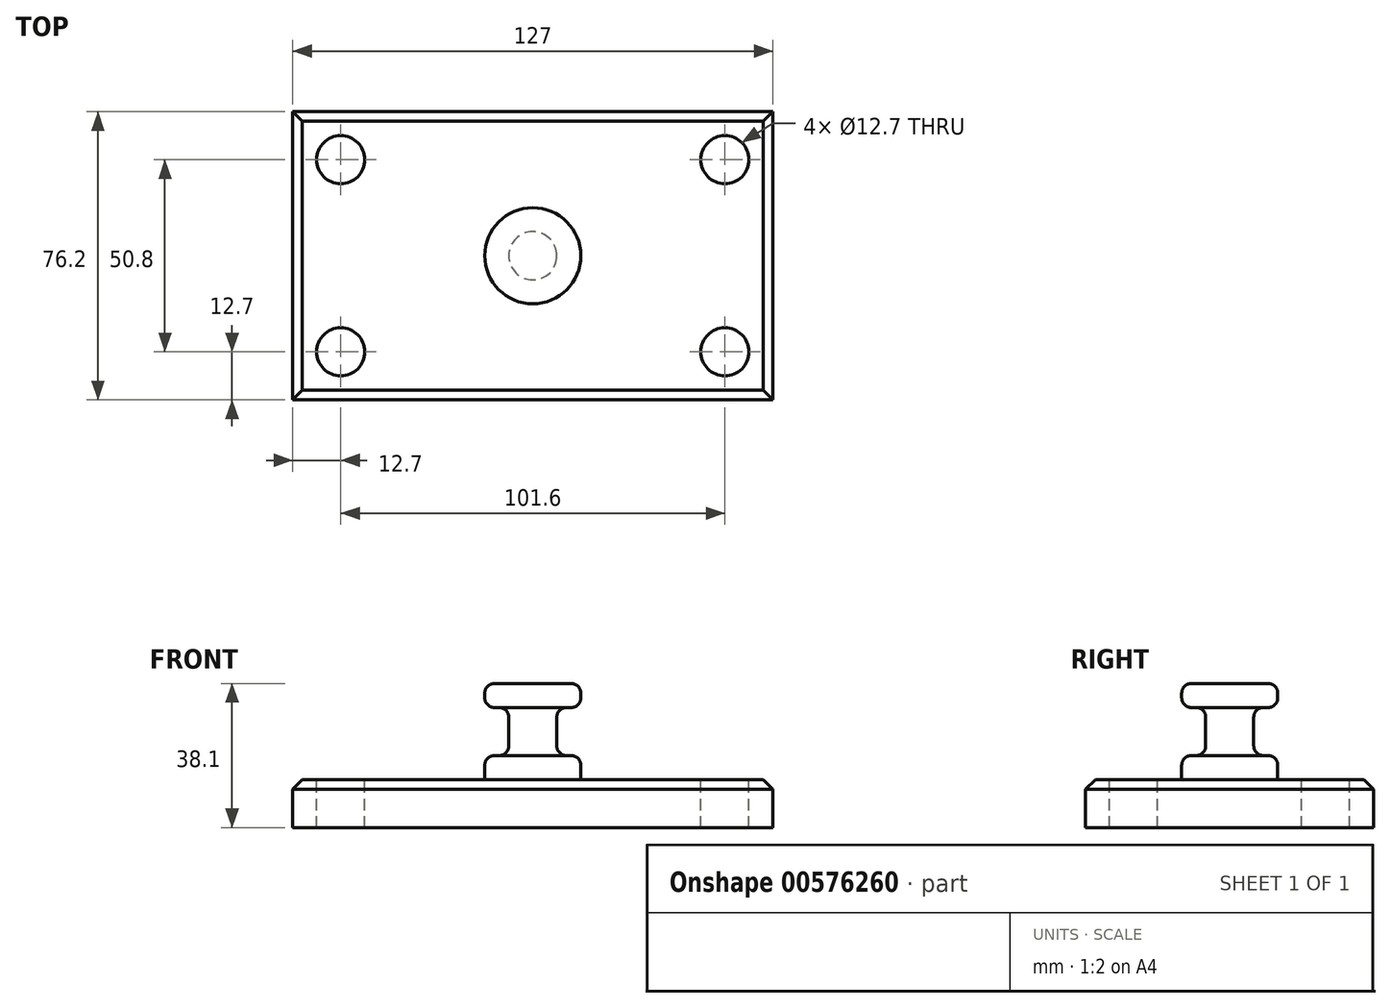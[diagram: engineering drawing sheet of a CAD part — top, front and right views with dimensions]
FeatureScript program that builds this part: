
annotation { "Feature Type Name" : "Feature", "Feature Type Description" : "" }
export const myFeature = defineFeature(function(context is Context, id is Id, definition is map)
    precondition{}
    {
        {
            var Q0;
            Q0=qCreatedBy(makeId("Top.planeOp"),FACE);
            var sketch = newSketch(context, id + "F0", { "sketchPlane" : qUnion([Q0])});
            skLineSegment(sketch, "E0.bottom", {"start": v(63.5, 38.1) * mm, "end": v(-63.5, 38.1) * mm});
            skLineSegment(sketch, "E0.top", {"start": v(63.5, -38.1) * mm, "end": v(-63.5, -38.1) * mm});
            skLineSegment(sketch, "E0.left", {"start": v(63.5, 38.1) * mm, "end": v(63.5, -38.1) * mm});
            skLineSegment(sketch, "E0.right", {"start": v(-63.5, 38.1) * mm, "end": v(-63.5, -38.1) * mm});
            skPoint(sketch, "E0.middle", {"position": v(0, 0) * mm});
            skSolve(sketch);
        }
        {
            var Q0;
            Q0=makeQuery(id+"F0.imprint","IMPRINT",FACE,{"disambiguationData":[TD([[makeQuery(id+"F0.imprint","IMPRINT",EDGE,{"derivedFrom":sQuery(id+"F0.wireOp",EDGE,"E0.bottom")}),1.0]])]});
            extrude(context, id + "F1", {"entities" : qUnion([Q0]), "endBound" : BoundingType.SYMMETRIC, "depth" : 12.7 * mm, "offsetDistance" : 25.4 * mm});
        }
        {
            var Q0;
            Q0=makeQuery(id+"F1.opExtrude","CAP_FACE",FACE,{"disambiguationData":[OSD([sQuery(id+"F0.wireOp",EDGE,"E0.bottom"),sQuery(id+"F0.wireOp",EDGE,"E0.top"),sQuery(id+"F0.wireOp",EDGE,"E0.left"),sQuery(id+"F0.wireOp",EDGE,"E0.right")])],"isStart":false});
            var sketch = newSketch(context, id + "F2", { "sketchPlane" : qUnion([Q0])});
            skPoint(sketch, "E1.middle", {"position": v(0, 0) * mm});
            skCircle(sketch, "E2", {"center": v(-50.8, 25.4) * mm, "radius": 6.35 * mm});
            skCircle(sketch, "E3", {"center": v(50.8, 25.4) * mm, "radius": 6.35 * mm});
            skCircle(sketch, "E4", {"center": v(50.8, -25.4) * mm, "radius": 6.35 * mm});
            skCircle(sketch, "E5", {"center": v(-50.8, -25.4) * mm, "radius": 6.35 * mm});
            skSolve(sketch);
        }
        {
            var Q0;
            Q0=makeQuery(id+"F2.imprint","IMPRINT",FACE,{"disambiguationData":[TD([[makeQuery(id+"F2.imprint","IMPRINT",EDGE,{"derivedFrom":sQuery(id+"F2.wireOp",EDGE,"E2")}),1.0]])]});
            var Q1;
            Q1=makeQuery(id+"F2.imprint","IMPRINT",FACE,{"disambiguationData":[TD([[makeQuery(id+"F2.imprint","IMPRINT",EDGE,{"derivedFrom":sQuery(id+"F2.wireOp",EDGE,"E3")}),1.0]])]});
            var Q2;
            Q2=makeQuery(id+"F2.imprint","IMPRINT",FACE,{"disambiguationData":[TD([[makeQuery(id+"F2.imprint","IMPRINT",EDGE,{"derivedFrom":sQuery(id+"F2.wireOp",EDGE,"E4")}),1.0]])]});
            var Q3;
            Q3=makeQuery(id+"F2.imprint","IMPRINT",FACE,{"disambiguationData":[TD([[makeQuery(id+"F2.imprint","IMPRINT",EDGE,{"derivedFrom":sQuery(id+"F2.wireOp",EDGE,"E5")}),1.0]])]});
            extrude(context, id + "F3", {"entities" : qUnion([Q0, Q1, Q2, Q3]), "operationType" : NewBodyOperationType.REMOVE, "oppositeDirection" : true, "depth" : 25.4 * mm, "offsetDistance" : 25.4 * mm});
        }
        {
            var Q0;
            Q0=qCreatedBy(makeId("Front.planeOp"),FACE);
            var sketch = newSketch(context, id + "F4", { "sketchPlane" : qUnion([Q0])});
            skLineSegment(sketch, "E6.bottom", {"start": v(0, 6.35) * mm, "end": v(12.7, 6.35) * mm});
            skLineSegment(sketch, "E6.top", {"start": v(0, 31.75) * mm, "end": v(12.7, 31.75) * mm});
            skLineSegment(sketch, "E6.left", {"start": v(0, 6.35) * mm, "end": v(0, 31.75) * mm});
            skLineSegment(sketch, "E6.right", {"start": v(12.7, 6.35) * mm, "end": v(12.7, 31.75) * mm});
            skSolve(sketch);
        }
        {
            var Q0;
            Q0=makeQuery(id+"F4.imprint","IMPRINT",FACE,{"disambiguationData":[TD([[makeQuery(id+"F4.imprint","IMPRINT",EDGE,{"derivedFrom":sQuery(id+"F4.wireOp",EDGE,"E6.bottom")}),1.0]])]});
            var Q1;
            Q1=sQuery(id+"F4.wireOp",EDGE,"E6.left");
            revolve(context, id + "F5", {"operationType" : NewBodyOperationType.ADD, "entities" : qUnion([Q0]), "axis" : qUnion([Q1]), "revolveType" : RevolveType.FULL});
        }
        {
            var Q0;
            Q0=qCreatedBy(makeId("Right.planeOp"),FACE);
            var sketch = newSketch(context, id + "F6", { "sketchPlane" : qUnion([Q0])});
            skLineSegment(sketch, "E7", {"start": v(0, 31.78) * mm, "end": v(0, 6.38) * mm});
            skLineSegment(sketch, "E8.bottom", {"start": v(6.35, 25.4) * mm, "end": v(19.05, 25.4) * mm});
            skLineSegment(sketch, "E8.top", {"start": v(6.35, 12.7) * mm, "end": v(19.05, 12.7) * mm});
            skLineSegment(sketch, "E8.left", {"start": v(6.35, 25.4) * mm, "end": v(6.35, 12.7) * mm});
            skLineSegment(sketch, "E8.right", {"start": v(19.05, 25.4) * mm, "end": v(19.05, 12.7) * mm});
            skSolve(sketch);
        }
        {
            var Q0;
            Q0=makeQuery(id+"F6.imprint","IMPRINT",FACE,{"disambiguationData":[TD([[makeQuery(id+"F6.imprint","IMPRINT",EDGE,{"derivedFrom":sQuery(id+"F6.wireOp",EDGE,"E8.bottom")}),-1.0]])]});
            var Q1;
            Q1=sQuery(id+"F6.wireOp",EDGE,"E7");
            revolve(context, id + "F7", {"operationType" : NewBodyOperationType.REMOVE, "entities" : qUnion([Q0]), "axis" : qUnion([Q1]), "revolveType" : RevolveType.FULL, "oppositeDirection" : true});
        }
        {
            var Q0;
            Q0=makeQuery(id+"F5.opRevolve","SWEPT_EDGE",EDGE,{"disambiguationData":[OSD([sQuery(id+"F4.wireOp",EDGE,"E6.top"),sQuery(id+"F4.wireOp",EDGE,"E6.right")])]});
            var Q1;
            Q1=makeQuery(id+"F5.opRevolve","SWEPT_EDGE",EDGE,{"disambiguationData":[OSD([sQuery(id+"F4.wireOp",EDGE,"E6.bottom"),sQuery(id+"F4.wireOp",EDGE,"E6.right")])]});
            fillet(context, id + "F8", {"entities" : qUnion([Q0, Q1]), "radius" : 2.54 * mm, "tangentPropagation" : true, "allowEdgeOverflow" : false});
        }
        {
            var Q0;
            Q0=makeQuery(id+"F1.opExtrude","CAP_EDGE",EDGE,{"disambiguationData":[OSD([sQuery(id+"F0.wireOp",EDGE,"E0.bottom")])],"isStart":false});
            var Q1;
            Q1=makeQuery(id+"F1.opExtrude","CAP_EDGE",EDGE,{"disambiguationData":[OSD([sQuery(id+"F0.wireOp",EDGE,"E0.right")])],"isStart":false});
            var Q2;
            Q2=makeQuery(id+"F1.opExtrude","CAP_EDGE",EDGE,{"disambiguationData":[OSD([sQuery(id+"F0.wireOp",EDGE,"E0.top")])],"isStart":false});
            var Q3;
            Q3=makeQuery(id+"F1.opExtrude","CAP_EDGE",EDGE,{"disambiguationData":[OSD([sQuery(id+"F0.wireOp",EDGE,"E0.left")])],"isStart":false});
            chamfer(context, id + "F9", {"entities" : qUnion([Q0, Q1, Q2, Q3]), "width" : 2.54 * mm, "tangentPropagation" : true});
        }
        {
            var Q0;
            Q0=makeQuery(id+"F7.boolean.opBoolean","INTERSECT",EDGE,{"derivedFrom":[makeQuery(id+"F5.opRevolve","SWEPT_FACE",FACE,{"disambiguationData":[OSD([sQuery(id+"F4.wireOp",EDGE,"E6.right")])]}),makeQuery(id+"F7.opRevolve","SWEPT_FACE",FACE,{"disambiguationData":[OSD([sQuery(id+"F6.wireOp",EDGE,"E8.bottom")])]})]});
            var Q1;
            Q1=makeQuery(id+"F7.boolean.opBoolean","INTERSECT",EDGE,{"derivedFrom":[makeQuery(id+"F5.opRevolve","SWEPT_FACE",FACE,{"disambiguationData":[OSD([sQuery(id+"F4.wireOp",EDGE,"E6.right")])]}),makeQuery(id+"F7.opRevolve","SWEPT_FACE",FACE,{"disambiguationData":[OSD([sQuery(id+"F6.wireOp",EDGE,"E8.top")])]})]});
            fillet(context, id + "F10", {"entities" : qUnion([Q0, Q1]), "radius" : 2.54 * mm, "tangentPropagation" : true, "allowEdgeOverflow" : false});
        }
        {
            var Q0;
            Q0=makeQuery(id+"F7.boolean.opBoolean","COPY",EDGE,{"derivedFrom":makeQuery(id+"F7.opRevolve","SWEPT_EDGE",EDGE,{"disambiguationData":[OSD([sQuery(id+"F6.wireOp",EDGE,"E8.top"),sQuery(id+"F6.wireOp",EDGE,"E8.left")])]})});
            var Q1;
            Q1=makeQuery(id+"F7.boolean.opBoolean","COPY",EDGE,{"derivedFrom":makeQuery(id+"F7.opRevolve","SWEPT_EDGE",EDGE,{"disambiguationData":[OSD([sQuery(id+"F6.wireOp",EDGE,"E8.bottom"),sQuery(id+"F6.wireOp",EDGE,"E8.left")])]})});
            fillet(context, id + "F11", {"entities" : qUnion([Q0, Q1]), "radius" : 2.54 * mm, "tangentPropagation" : true, "allowEdgeOverflow" : false});
        }
    });
